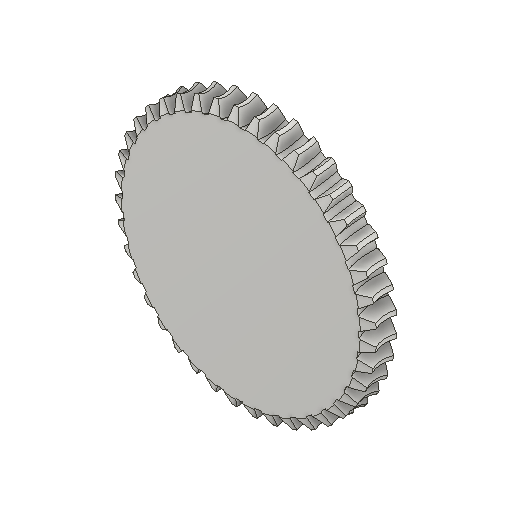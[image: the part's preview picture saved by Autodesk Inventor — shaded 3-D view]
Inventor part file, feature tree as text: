
AUTODESK INVENTOR PART (.ipt)
format: ipt  version: 2024.1 (Build 281209000, 209)  size: 603,136 bytes
history: native  units: mm (DEFAULTED — no unit token found)
features: other x8, plane x3, pattern_circular x1
ambient origin geometry x5: Origin, X Axis, Y Axis, Z Axis, Center Point
bodies: Solid1 (feature_tree)
feature tree (12):
  other  "Zahnebene"
  other  "Grundkörperskizze"
  other  "Grundkörper"
  other  "Grundkörper2"
  plane  "Work Plane13"
  other  "Zahn"
  pattern_circular  "Zahnanordnung"  Angle=90.0deg  [1 undecoded]
  plane  "Work Plane14"
  plane  "Work Plane15"
  other  "Zahnskizze"
  other  "Srf1"
  other  "Flankendurchmesser"
note: 1 required parameter value undecoded (feature->parameter linkage not recoverable at this tier; creation-order binding heuristic only, values carry confidence <= 0.55)
